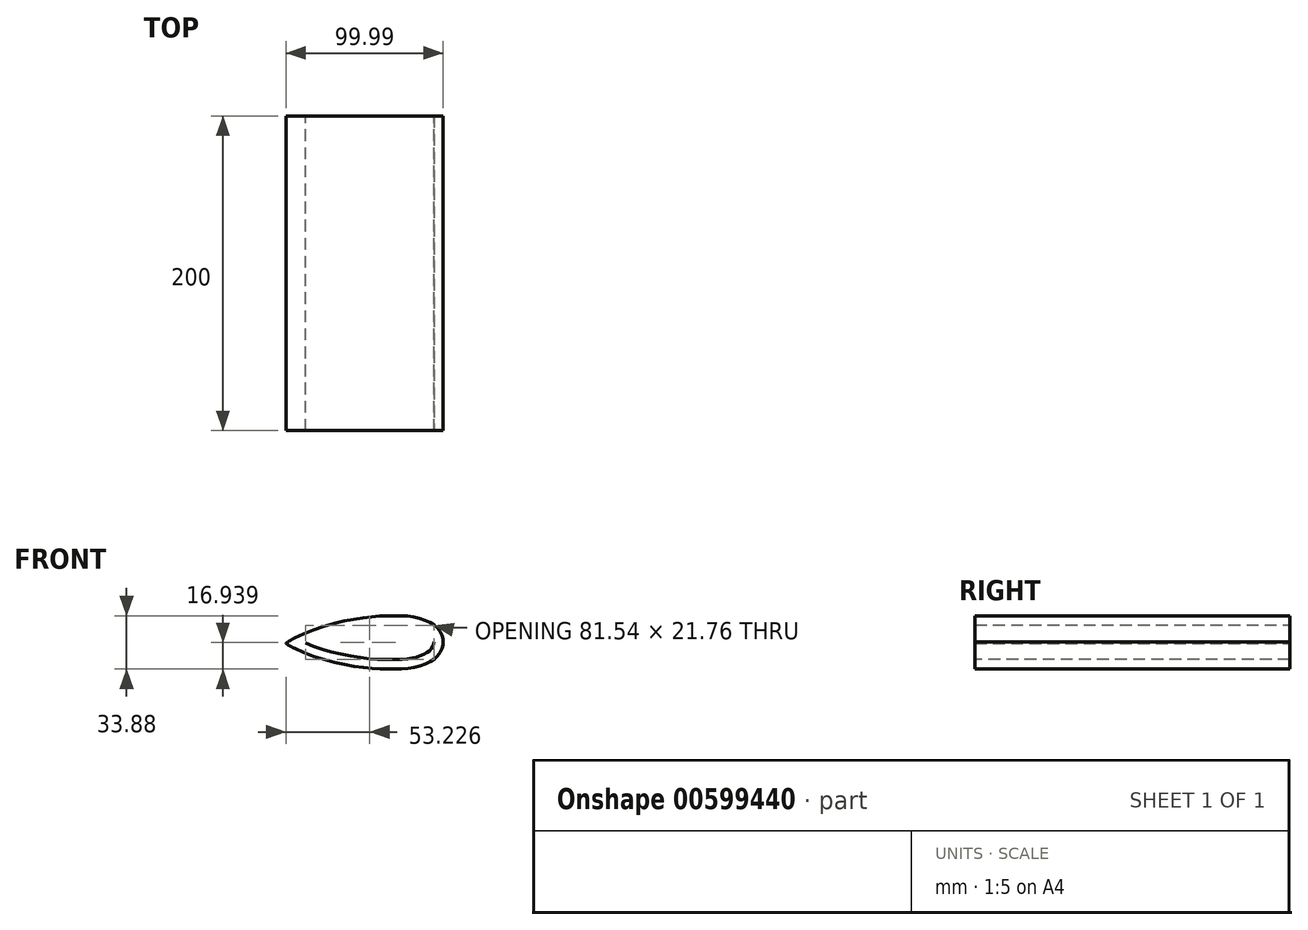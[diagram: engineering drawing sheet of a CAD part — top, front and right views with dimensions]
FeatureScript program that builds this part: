
annotation { "Feature Type Name" : "Feature", "Feature Type Description" : "" }
export const myFeature = defineFeature(function(context is Context, id is Id, definition is map)
    precondition{}
    {
        {
            var Q0;
            Q0=qCreatedBy(makeId("Front.planeOp"),FACE);
            var sketch = newSketch(context, id + "F0", { "sketchPlane" : qUnion([Q0])});
            skFitSpline(sketch, "E0", {"points": [v(-56.66, -0.49) * mm, v(-29.02, 11.29) * mm, v(-1.4, 16.48) * mm, v(15.1, 17.01) * mm, v(27, 15.78) * mm, v(36.04, 12.06) * mm, v(40.32, 8.33) * mm, v(42.98, 3.38) * mm, v(43.33, 0.42) * mm], "startDerivative": vector(96, 70.54) * mm, "endDerivative": vector(0.85, -43.4) * mm});
            skFitSpline(sketch, "E1.MirrorCS", {"points": [v(-56.66, -0.49) * mm, v(-28.81, -11.76) * mm, v(-1.1, -16.45) * mm, v(15.4, -16.68) * mm, v(27.28, -15.23) * mm, v(36.26, -11.35) * mm, v(40.47, -7.54) * mm, v(43.04, -2.54) * mm, v(43.33, 0.42) * mm], "startDerivative": vector(97.27, -68.79) * mm, "endDerivative": vector(0.07, 43.4) * mm});
            skFitSpline(sketch, "E2.0", {"points": [v(-53.1, -5.32) * mm, v(-52.31, -4.74) * mm, v(-50.42, -3.5) * mm, v(-46.86, -1.6) * mm, v(-42.76, 0.25) * mm, v(-38.28, 2.02) * mm, v(-33.56, 3.66) * mm, v(-28.74, 5.15) * mm, v(-23.98, 6.46) * mm, v(-17.78, 7.95) * mm, v(-11.82, 9.1) * mm, v(-6.21, 9.92) * mm, v(-2.2, 10.4) * mm, v(1.57, 10.72) * mm, v(5.14, 10.93) * mm, v(8.53, 11.04) * mm, v(11.24, 11.06) * mm, v(13.35, 11.04) * mm, v(14.65, 11.02) * mm, v(15.68, 11) * mm, v(16.68, 10.97) * mm, v(18.4, 10.9) * mm, v(20.24, 10.79) * mm, v(21.97, 10.6) * mm, v(23.23, 10.43) * mm, v(24.23, 10.25) * mm, v(25.01, 10.08) * mm, v(25.59, 9.95) * mm, v(26.16, 9.8) * mm, v(26.93, 9.58) * mm, v(27.88, 9.27) * mm, v(29, 8.86) * mm, v(30.07, 8.42) * mm, v(31.08, 7.95) * mm, v(32, 7.47) * mm, v(32.7, 7.08) * mm, v(33.18, 6.78) * mm, v(33.62, 6.5) * mm, v(34.09, 6.16) * mm, v(34.55, 5.78) * mm, v(34.95, 5.4) * mm, v(35.27, 5.04) * mm, v(35.53, 4.71) * mm, v(35.8, 4.35) * mm, v(36.16, 3.85) * mm, v(36.54, 3.2) * mm, v(36.82, 2.7) * mm, v(36.99, 2.32) * mm, v(37.1, 2.07) * mm, v(37.17, 1.86) * mm, v(37.21, 1.73) * mm, v(37.23, 1.66) * mm, v(37.25, 1.6) * mm, v(37.27, 1.51) * mm, v(37.28, 1.4) * mm, v(37.3, 1.23) * mm, v(37.32, 0.93) * mm, v(37.33, 0.54) * mm, v(37.34, 0.3) * mm]});
            skFitSpline(sketch, "E2.1", {"points": [v(-53.2, 4.41) * mm, v(-52.39, 3.84) * mm, v(-50.47, 2.64) * mm, v(-46.88, 0.81) * mm, v(-42.75, -0.97) * mm, v(-38.23, -2.66) * mm, v(-33.49, -4.22) * mm, v(-28.64, -5.62) * mm, v(-23.86, -6.84) * mm, v(-17.63, -8.22) * mm, v(-11.66, -9.25) * mm, v(-6.03, -9.98) * mm, v(-2.02, -10.38) * mm, v(1.77, -10.64) * mm, v(5.34, -10.79) * mm, v(8.73, -10.83) * mm, v(11.44, -10.8) * mm, v(13.55, -10.75) * mm, v(14.85, -10.7) * mm, v(15.88, -10.66) * mm, v(16.88, -10.61) * mm, v(18.59, -10.52) * mm, v(20.43, -10.37) * mm, v(22.16, -10.15) * mm, v(23.41, -9.95) * mm, v(24.41, -9.76) * mm, v(25.2, -9.58) * mm, v(25.76, -9.43) * mm, v(26.33, -9.27) * mm, v(27.1, -9.04) * mm, v(28.04, -8.71) * mm, v(29.15, -8.28) * mm, v(30.22, -7.81) * mm, v(31.22, -7.33) * mm, v(32.14, -6.83) * mm, v(32.82, -6.43) * mm, v(33.3, -6.12) * mm, v(33.73, -5.83) * mm, v(34.2, -5.48) * mm, v(34.64, -5.1) * mm, v(35.04, -4.7) * mm, v(35.36, -4.34) * mm, v(35.61, -4.01) * mm, v(35.88, -3.65) * mm, v(36.22, -3.14) * mm, v(36.6, -2.5) * mm, v(36.86, -1.97) * mm, v(37.02, -1.6) * mm, v(37.13, -1.34) * mm, v(37.2, -1.13) * mm, v(37.24, -1) * mm, v(37.26, -0.93) * mm, v(37.27, -0.86) * mm, v(37.29, -0.78) * mm, v(37.3, -0.67) * mm, v(37.32, -0.5) * mm, v(37.33, -0.2) * mm, v(37.33, 0.2) * mm, v(37.33, 0.43) * mm]});
            skSolve(sketch);
        }
        {
            var Q0;
            Q0 = qSketchRegion(id + "F0", true);
            extrude(context, id + "F1", {"entities" : qUnion([Q0]), "depth" : 200 * mm, "offsetDistance" : 25 * mm});
        }
    });
